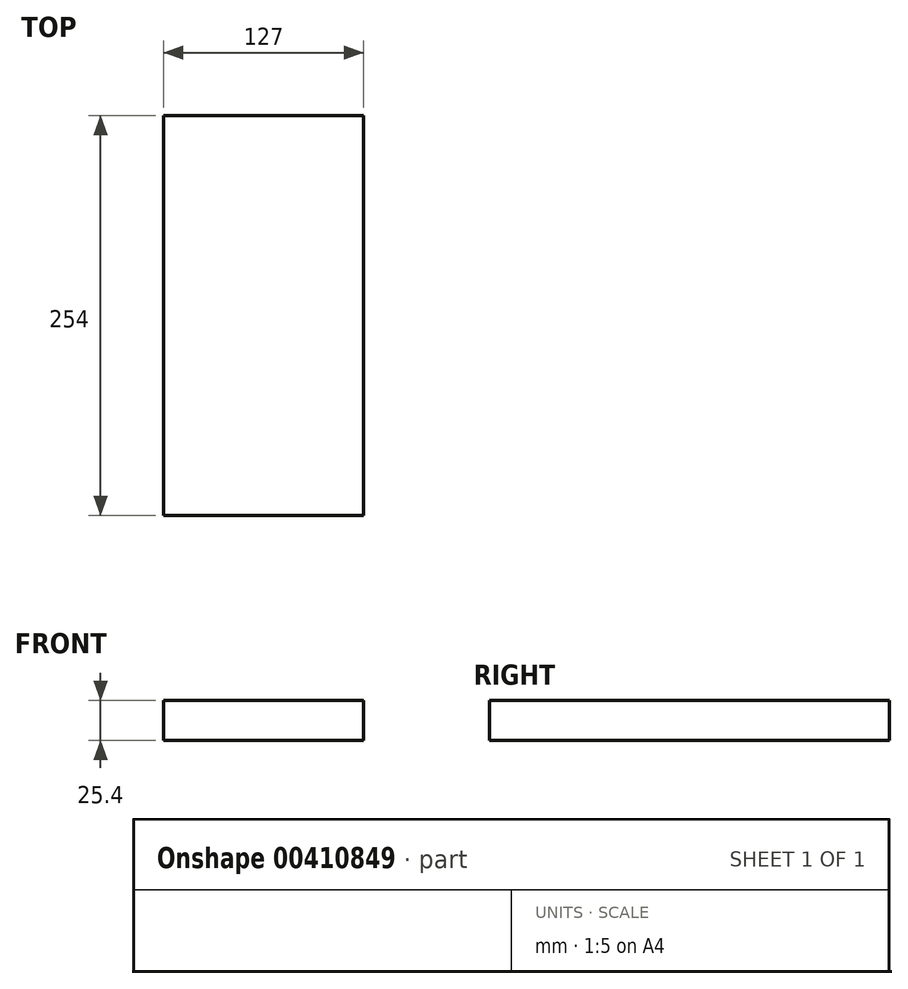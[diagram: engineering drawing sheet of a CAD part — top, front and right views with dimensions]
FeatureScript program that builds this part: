
annotation { "Feature Type Name" : "Feature", "Feature Type Description" : "" }
export const myFeature = defineFeature(function(context is Context, id is Id, definition is map)
    precondition{}
    {
        {
            var Q0;
            Q0=qCreatedBy(makeId("Front.planeOp"),FACE);
            var sketch = newSketch(context, id + "F0", { "sketchPlane" : qUnion([Q0])});
            skLineSegment(sketch, "E0", {"start": v(-55.67, -6.87) * mm, "end": v(-55.67, -32.27) * mm});
            skLineSegment(sketch, "E1", {"start": v(-55.67, -32.27) * mm, "end": v(71.33, -32.27) * mm});
            skLineSegment(sketch, "E2", {"start": v(71.33, -32.27) * mm, "end": v(71.33, -6.87) * mm});
            skLineSegment(sketch, "E3", {"start": v(71.33, -6.87) * mm, "end": v(-55.67, -6.87) * mm});
            skSolve(sketch);
        }
        {
            var Q0;
            Q0=makeQuery(id+"F0.imprint","IMPRINT",FACE,{"disambiguationData":[TD([[makeQuery(id+"F0.imprint","IMPRINT",EDGE,{"derivedFrom":sQuery(id+"F0.wireOp",EDGE,"E0")}),1.0]])]});
            extrude(context, id + "F1", {"entities" : qUnion([Q0]), "depth" : 254 * mm});
        }
    });
